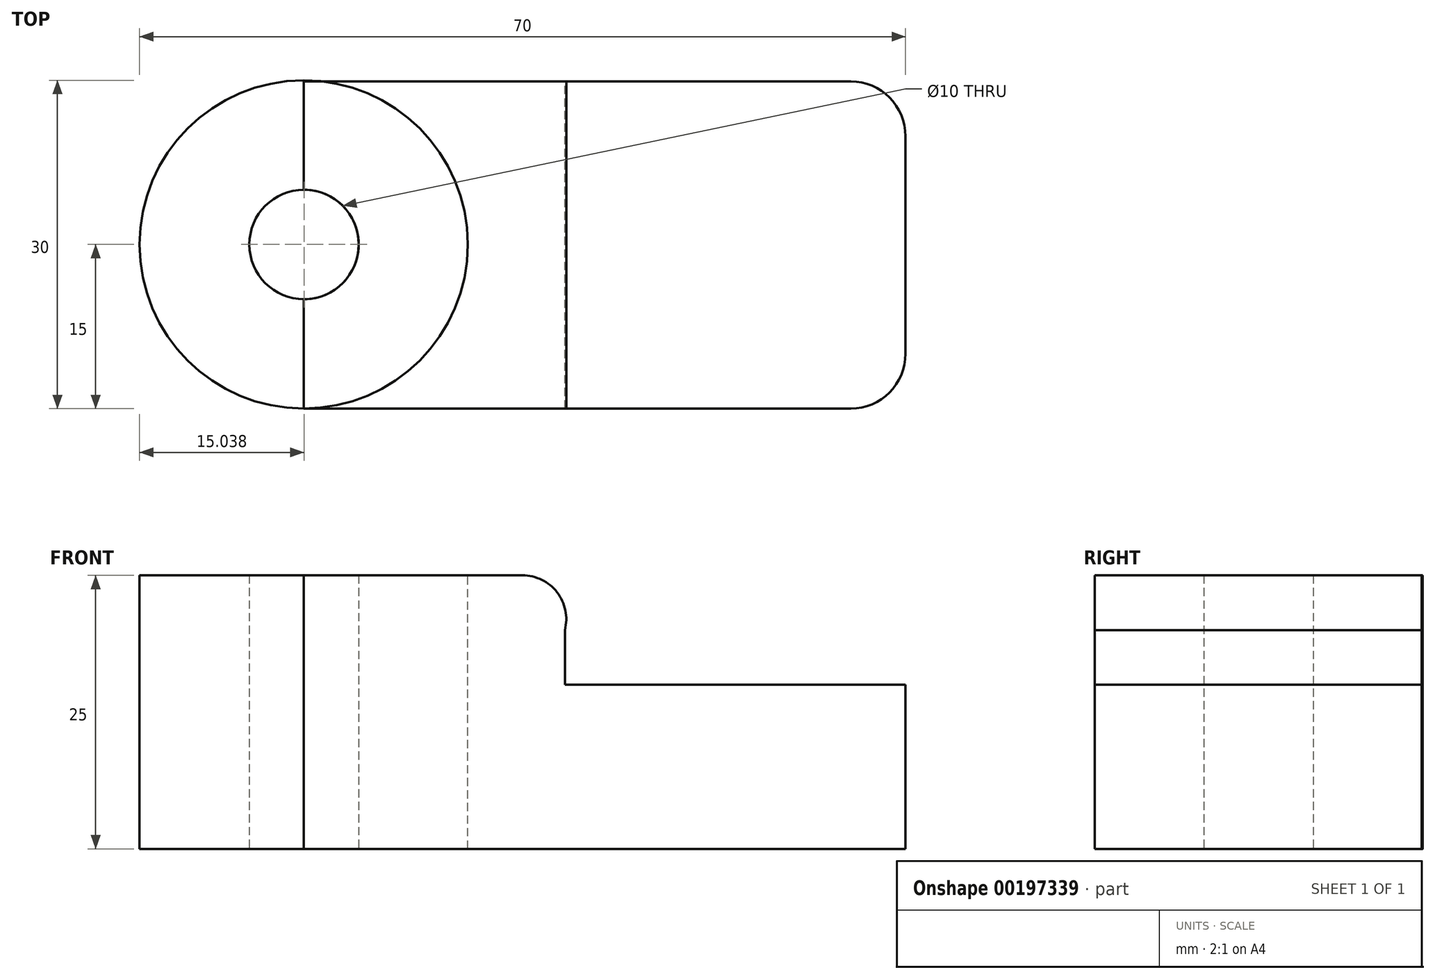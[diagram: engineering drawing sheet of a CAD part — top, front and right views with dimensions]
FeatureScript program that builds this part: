
annotation { "Feature Type Name" : "Feature", "Feature Type Description" : "" }
export const myFeature = defineFeature(function(context is Context, id is Id, definition is map)
    precondition{}
    {
        {
            var Q0;
            Q0=qCreatedBy(makeId("Front.planeOp"),FACE);
            var sketch = newSketch(context, id + "F0", { "sketchPlane" : qUnion([Q0])});
            skLineSegment(sketch, "E0.bottom", {"start": v(-35.14, 15) * mm, "end": v(4.86, 15) * mm});
            skLineSegment(sketch, "E0.top", {"start": v(-35.14, 0) * mm, "end": v(4.86, 0) * mm});
            skLineSegment(sketch, "E0.left", {"start": v(-35.14, 15) * mm, "end": v(-35.14, 0) * mm});
            skLineSegment(sketch, "E0.right", {"start": v(4.86, 15) * mm, "end": v(4.86, 0) * mm});
            skLineSegment(sketch, "E1.bottom", {"start": v(-50.14, 25) * mm, "end": v(-35.14, 25) * mm});
            skLineSegment(sketch, "E1.top", {"start": v(-50.14, 0) * mm, "end": v(-35.14, 0) * mm});
            skLineSegment(sketch, "E1.left", {"start": v(-50.14, 25) * mm, "end": v(-50.14, 0) * mm});
            skLineSegment(sketch, "E1.right", {"start": v(-35.14, 25) * mm, "end": v(-35.14, 0) * mm});
            skLineSegment(sketch, "E2", {"start": v(-35.14, 25) * mm, "end": v(-30.14, 25) * mm});
            skArc(sketch, "E3", {"start": v(-30.14, 25) * mm, "mid": v(-26.97, 23.45) * mm, "end": v(-26.26, 20) * mm});
            skLineSegment(sketch, "E4", {"start": v(-26.26, 20) * mm, "end": v(-26.26, 15) * mm});
            skSolve(sketch);
        }
        {
            var Q0;
            {var subQ2=sQuery(id+"F0.wireOp",EDGE,"E1.bottom");Q0=makeQuery(id+"F0.imprint","IMPRINT",FACE,{"disambiguationData":[TD([[makeQuery(id+"F0.imprint","IMPRINT",EDGE,{"derivedFrom":subQ2}),-1.0]])]});}
            var Q1;
            Q1=sQuery(id+"F0.wireOp",EDGE,"E1.left");
            revolve(context, id + "F1", {"entities" : qUnion([Q0]), "axis" : qUnion([Q1]), "revolveType" : RevolveType.FULL});
        }
        {
            var Q0;
            {var subQ1=sQuery(id+"F0.wireOp",EDGE,"E0.top");Q0=makeQuery(id+"F0.imprint","IMPRINT",FACE,{"disambiguationData":[TD([[makeQuery(id+"F0.imprint","IMPRINT",EDGE,{"derivedFrom":subQ1}),1.0]])]});}
            var Q1;
            {var subQ0=sQuery(id+"F0.wireOp",EDGE,"E2");Q1=makeQuery(id+"F0.imprint","IMPRINT",FACE,{"disambiguationData":[TD([[makeQuery(id+"F0.imprint","IMPRINT",EDGE,{"derivedFrom":subQ0}),-1.0]])]});}
            var Q2;
            {var subQ2=sQuery(id+"F0.wireOp",EDGE,"E1.bottom");Q2=makeQuery(id+"F0.imprint","IMPRINT",FACE,{"disambiguationData":[TD([[makeQuery(id+"F0.imprint","IMPRINT",EDGE,{"derivedFrom":subQ2}),-1.0]])]});}
            extrude(context, id + "F2", {"entities" : qUnion([Q0, Q1, Q2]), "depth" : 15 * mm, "hasSecondDirection" : true, "secondDirectionOppositeDirection" : true, "secondDirectionDepth" : 14.9 * mm});
        }
        {
            var Q0;
            Q0=qCreatedBy(makeId("Top.planeOp"),FACE);
            var sketch = newSketch(context, id + "F3", { "sketchPlane" : qUnion([Q0])});
            skCircle(sketch, "E5", {"center": v(-50.1, 0) * mm, "radius": 4.85 * mm});
            skSolve(sketch);
        }
        {
            var Q0;
            Q0=sQuery(id+"F3.wireOp",VERTEX,"E5.center");
            var Q1;
            Q1=makeQuery(id+"F1.opRevolve","SWEPT_BODY",BODY,{"disambiguationData":[OSD([sQuery(id+"F0.wireOp",EDGE,"E1.bottom"),sQuery(id+"F0.wireOp",EDGE,"E1.top"),sQuery(id+"F0.wireOp",EDGE,"E1.left"),sQuery(id+"F0.wireOp",EDGE,"E1.right")])]});
            var Q2;
            Q2=makeQuery(id+"F2.opExtrude","SWEPT_BODY",BODY,{"disambiguationData":[OSD([sQuery(id+"F0.wireOp",EDGE,"E0.bottom"),sQuery(id+"F0.wireOp",EDGE,"E0.top"),sQuery(id+"F0.wireOp",EDGE,"E0.right"),sQuery(id+"F0.wireOp",EDGE,"E1.bottom"),sQuery(id+"F0.wireOp",EDGE,"E1.top"),sQuery(id+"F0.wireOp",EDGE,"E1.left"),sQuery(id+"F0.wireOp",EDGE,"E2"),sQuery(id+"F0.wireOp",EDGE,"E3"),sQuery(id+"F0.wireOp",EDGE,"E4")])]});
            hole(context, id + "F4", {"style" : HoleStyle.SIMPLE, "endStyle" : HoleEndStyle.THROUGH, "oppositeDirection" : true, "holeDiameter" : 10 * mm, "locations" : qUnion([Q0]), "scope" : qUnion([Q1, Q2]), "isTappedThrough" : true});
        }
        {
            var Q0;
            Q0=makeQuery(id+"F2.opExtrude","CAP_EDGE",EDGE,{"disambiguationData":[OSD([sQuery(id+"F0.wireOp",EDGE,"E0.right")])],"isStart":true});
            var Q1;
            Q1=makeQuery(id+"F2.opExtrude","CAP_EDGE",EDGE,{"disambiguationData":[OSD([sQuery(id+"F0.wireOp",EDGE,"E0.right")])],"isStart":false});
            fillet(context, id + "F5", {"entities" : qUnion([Q0, Q1]), "radius" : 5 * mm, "tangentPropagation" : true, "allowEdgeOverflow" : false});
        }
    });
